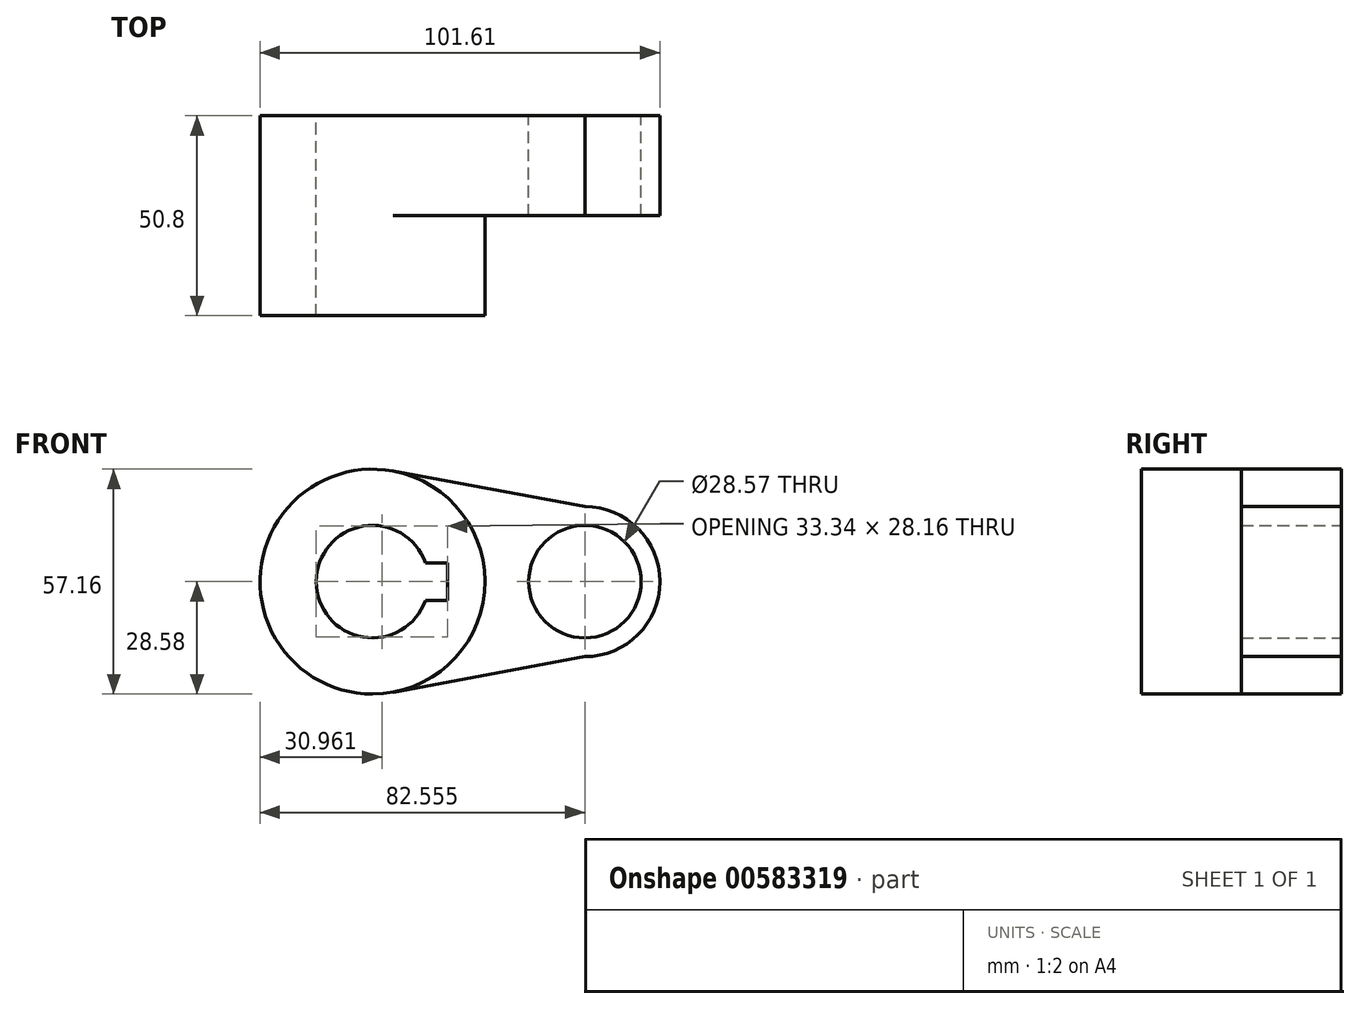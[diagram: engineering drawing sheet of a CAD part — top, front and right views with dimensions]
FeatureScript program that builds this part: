
annotation { "Feature Type Name" : "Feature", "Feature Type Description" : "" }
export const myFeature = defineFeature(function(context is Context, id is Id, definition is map)
    precondition{}
    {
        {
            var Q0;
            Q0=qCreatedBy(makeId("Front.planeOp"),FACE);
            var sketch = newSketch(context, id + "F0", { "sketchPlane" : qUnion([Q0])});
            skCircle(sketch, "E0", {"center": v(0, 0) * mm, "radius": 28.58 * mm});
            skCircle(sketch, "E1", {"center": v(53.98, 0) * mm, "radius": 19.05 * mm});
            skLineSegment(sketch, "E2", {"start": v(5.21, 28.1) * mm, "end": v(53.98, 19.05) * mm});
            skLineSegment(sketch, "E3", {"start": v(5.21, -28.1) * mm, "end": v(53.98, -19.05) * mm});
            skCircle(sketch, "E4", {"center": v(0, 0) * mm, "radius": 14.29 * mm});
            skCircle(sketch, "E5", {"center": v(53.98, 0) * mm, "radius": 14.29 * mm});
            skLineSegment(sketch, "E6.bottom", {"start": v(19.05, -4.76) * mm, "end": v(-19.05, -4.76) * mm});
            skLineSegment(sketch, "E6.top", {"start": v(19.05, 4.76) * mm, "end": v(-19.05, 4.76) * mm});
            skLineSegment(sketch, "E6.left", {"start": v(19.05, -4.76) * mm, "end": v(19.05, 4.76) * mm});
            skLineSegment(sketch, "E6.right", {"start": v(-19.05, -4.76) * mm, "end": v(-19.05, 4.76) * mm});
            skSolve(sketch);
        }
        {
            var Q0;
            {var subQ7=sQuery(id+"F0.wireOp",EDGE,"E6.left");Q0=makeQuery(id+"F0.imprint","IMPRINT",FACE,{"disambiguationData":[TD([[makeQuery(id+"F0.imprint","IMPRINT",EDGE,{"derivedFrom":subQ7}),-1.0]])]});}
            var Q1;
            {var subQ0=sQuery(id+"F0.wireOp",EDGE,"E2");Q1=makeQuery(id+"F0.imprint","IMPRINT",FACE,{"disambiguationData":[TD([[makeQuery(id+"F0.imprint","IMPRINT",EDGE,{"derivedFrom":subQ0}),-1.0]])]});}
            var Q2;
            Q2=makeQuery(id+"F0.imprint","IMPRINT",FACE,{"disambiguationData":[TD([[makeQuery(id+"F0.imprint","IMPRINT",EDGE,{"derivedFrom":sQuery(id+"F0.wireOp",EDGE,"E5")}),-1.0]])]});
            extrude(context, id + "F1", {"entities" : qUnion([Q0, Q1, Q2]), "depth" : 25.4 * mm, "offsetDistance" : 25.4 * mm});
        }
        {
            var Q0;
            {var subQ7=sQuery(id+"F0.wireOp",EDGE,"E6.left");Q0=makeQuery(id+"F0.imprint","IMPRINT",FACE,{"disambiguationData":[TD([[makeQuery(id+"F0.imprint","IMPRINT",EDGE,{"derivedFrom":subQ7}),-1.0]])]});}
            extrude(context, id + "F2", {"entities" : qUnion([Q0]), "operationType" : NewBodyOperationType.ADD, "depth" : 50.8 * mm, "offsetDistance" : 25.4 * mm});
        }
        {
            var Q0;
            {var subQ5=sQuery(id+"F0.wireOp",EDGE,"E6.right");Q0=makeQuery(id+"F0.imprint","IMPRINT",FACE,{"disambiguationData":[TD([[makeQuery(id+"F0.imprint","IMPRINT",EDGE,{"derivedFrom":subQ5}),-1.0]])]});}
            extrude(context, id + "F3", {"entities" : qUnion([Q0]), "operationType" : NewBodyOperationType.ADD, "depth" : 50.8 * mm, "offsetDistance" : 25.4 * mm});
        }
    });
